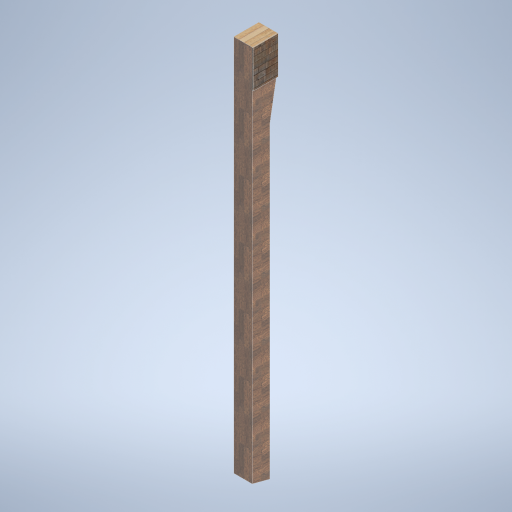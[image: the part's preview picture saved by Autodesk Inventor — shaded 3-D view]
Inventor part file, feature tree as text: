
AUTODESK INVENTOR PART (.ipt)
format: ipt  version: 2024.2 (Build 282272000, 272)  size: 314,880 bytes
history: native  units: in
note: dims shown in document units (in); Inventor stores cm internally (conversion verified against a paired STEP export)
features: other x3, sketch x1
ambient origin geometry x8: Origin, YZ Plane, XZ Plane, XY Plane, X Axis, Y Axis, Z Axis, Center Point
bodies: Solid1 (feature_tree)
feature tree (4):
  other  "side_pillar_02_MIR.ipt"
  other  "Solid1::side_pillar_02_MIR.ipt"
  other  "TaggingFeature1"
  sketch  "Sketch3"  dims[d0=0.3937in]
